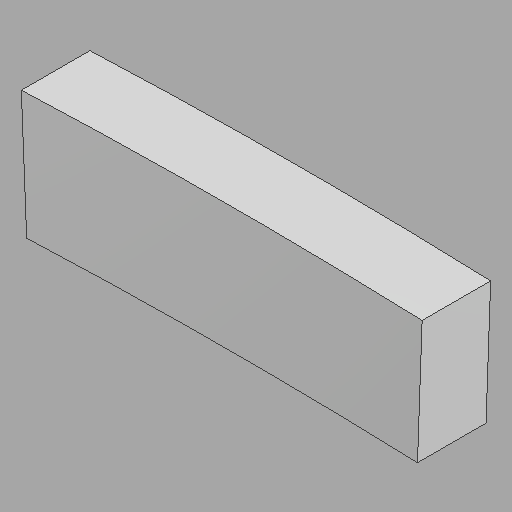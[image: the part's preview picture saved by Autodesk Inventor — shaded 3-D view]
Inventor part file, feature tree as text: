
AUTODESK INVENTOR PART (.ipt)
format: ipt  version: 2022.1 (Build 261234020, 234B)  size: 89,600 bytes
history: imported  units: in
note: dims shown in document units (in); Inventor stores cm internally (conversion verified against a paired STEP export)
features: imported_body x1
ambient origin geometry x8: Origin, YZ Plane, XZ Plane, XY Plane, X Axis, Y Axis, Z Axis, Center Point
bodies: Solid1 (imported_parasolid)
feature tree (1):
  imported_body  NMx_Import_Brep_tag  [imported B-rep: ~7 faces, bbox_mm=[891.325055, 281.320708, 152.4]]
